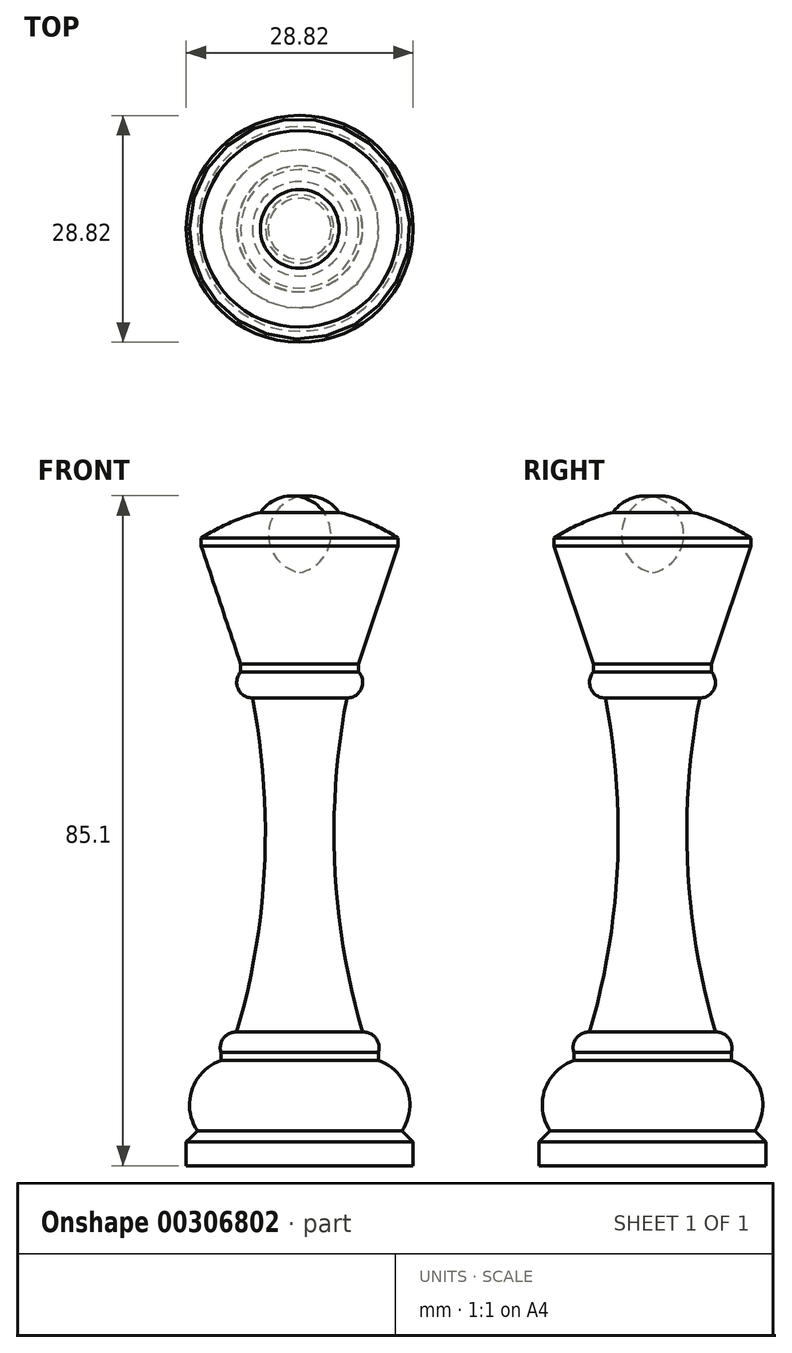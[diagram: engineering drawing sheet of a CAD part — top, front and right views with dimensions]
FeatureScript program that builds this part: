
annotation { "Feature Type Name" : "Feature", "Feature Type Description" : "" }
export const myFeature = defineFeature(function(context is Context, id is Id, definition is map)
    precondition{}
    {
        {
            var Q0;
            Q0=qCreatedBy(makeId("Front.planeOp"),FACE);
            var sketch = newSketch(context, id + "F0", { "sketchPlane" : qUnion([Q0])});
            skArc(sketch, "E0", {"start": v(5, -2) * mm, "mid": v(2.8, -0.26) * mm, "end": v(0, 0) * mm});
            skArc(sketch, "E1", {"start": v(12.5, -5.27) * mm, "mid": v(8.88, -3.33) * mm, "end": v(5, -2) * mm});
            skLineSegment(sketch, "E2", {"start": v(12.5, -5.27) * mm, "end": v(12.5, -6.27) * mm});
            skLineSegment(sketch, "E3", {"start": v(12.5, -6.27) * mm, "end": v(7.5, -21.27) * mm});
            skLineSegment(sketch, "E4", {"start": v(7.5, -21.27) * mm, "end": v(7.5, -22.27) * mm});
            skArc(sketch, "E5", {"start": v(6, -25.6) * mm, "mid": v(7.82, -24.42) * mm, "end": v(7.5, -22.27) * mm});
            skArc(sketch, "E6", {"start": v(6, -25.6) * mm, "mid": v(4.46, -46.93) * mm, "end": v(8, -68.02) * mm});
            skArc(sketch, "E7", {"start": v(10, -70.62) * mm, "mid": v(9.67, -68.8) * mm, "end": v(8, -68.02) * mm});
            skLineSegment(sketch, "E8", {"start": v(10, -70.62) * mm, "end": v(10, -71.62) * mm});
            skArc(sketch, "E9", {"start": v(13, -80.59) * mm, "mid": v(13.7, -75.37) * mm, "end": v(10, -71.62) * mm});
            skLineSegment(sketch, "E10", {"start": v(13, -80.59) * mm, "end": v(14.41, -82) * mm});
            skLineSegment(sketch, "E11", {"start": v(14.41, -82) * mm, "end": v(14.41, -85) * mm});
            skLineSegment(sketch, "E12", {"start": v(14.41, -85) * mm, "end": v(0, -85) * mm});
            skLineSegment(sketch, "E13", {"start": v(0, -85) * mm, "end": v(0, 0) * mm});
            skSolve(sketch);
        }
        {
            var Q0;
            Q0=makeQuery(id+"F0.imprint","IMPRINT",FACE,{"disambiguationData":[TD([[makeQuery(id+"F0.imprint","IMPRINT",EDGE,{"derivedFrom":sQuery(id+"F0.wireOp",EDGE,"E0")}),1.0]])]});
            var Q1;
            Q1=sQuery(id+"F0.wireOp",EDGE,"E13");
            revolve(context, id + "F1", {"entities" : qUnion([Q0]), "axis" : qUnion([Q1]), "revolveType" : RevolveType.FULL});
        }
    });
